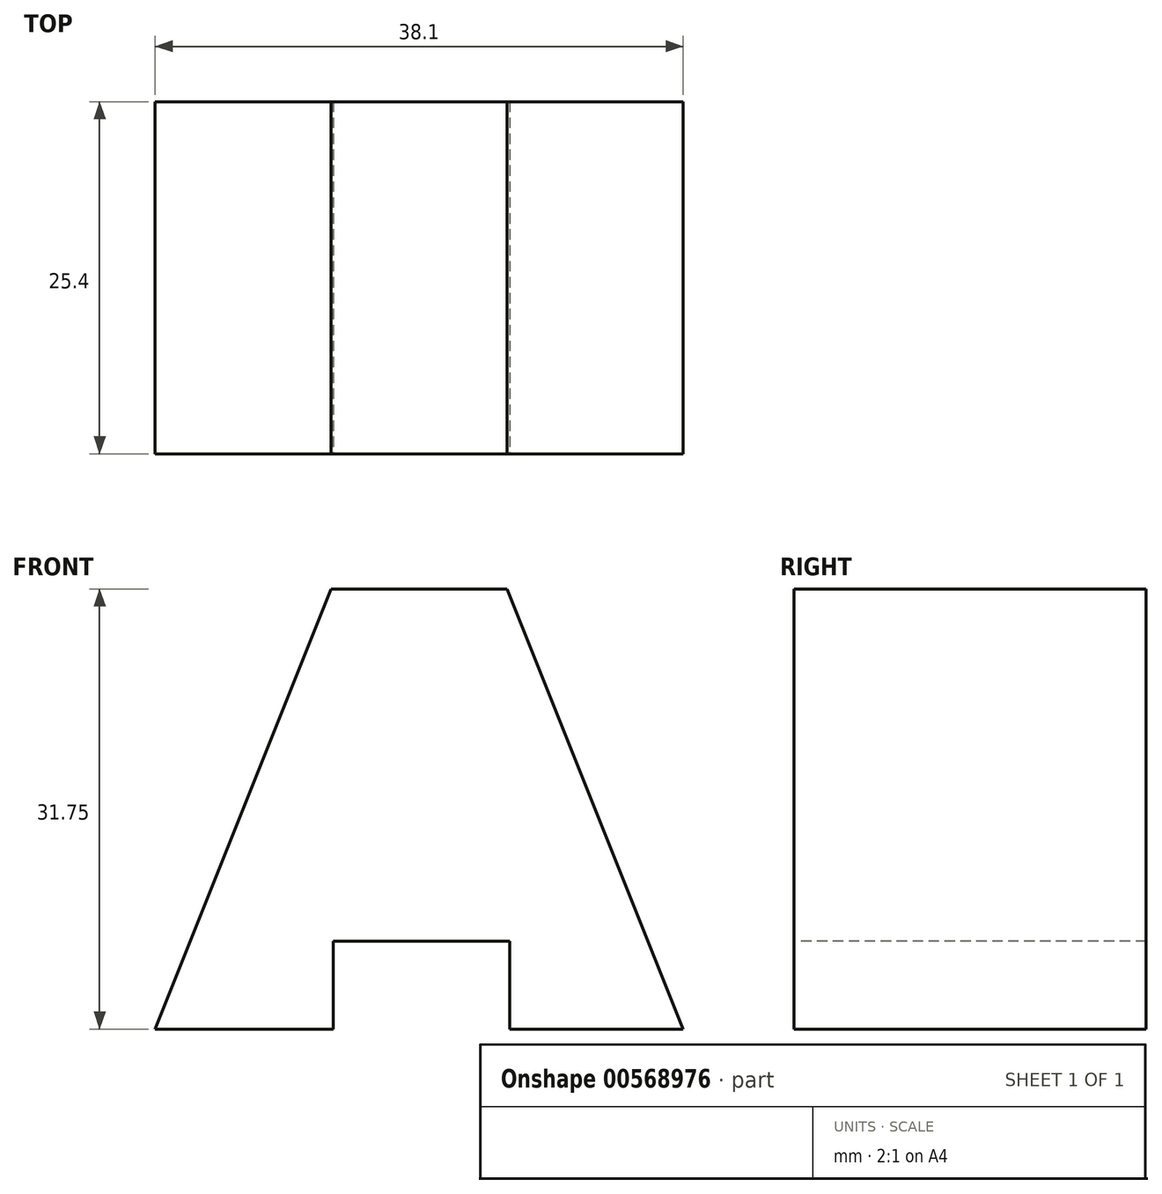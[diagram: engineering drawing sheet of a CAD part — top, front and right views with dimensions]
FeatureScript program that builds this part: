
annotation { "Feature Type Name" : "Feature", "Feature Type Description" : "" }
export const myFeature = defineFeature(function(context is Context, id is Id, definition is map)
    precondition{}
    {
        {
            var Q0;
            Q0=qCreatedBy(makeId("Front.planeOp"),FACE);
            var sketch = newSketch(context, id + "F0", { "sketchPlane" : qUnion([Q0])});
            skLineSegment(sketch, "E0.bottom", {"start": v(-30.4, 31.75) * mm, "end": v(7.7, 31.75) * mm});
            skLineSegment(sketch, "E0.top", {"start": v(-30.4, 0) * mm, "end": v(7.7, 0) * mm});
            skLineSegment(sketch, "E0.left", {"start": v(-30.4, 31.75) * mm, "end": v(-30.4, 0) * mm});
            skLineSegment(sketch, "E0.right", {"start": v(7.7, 31.75) * mm, "end": v(7.7, 0) * mm});
            skSolve(sketch);
        }
        {
            var Q0;
            Q0 = qSketchRegion(id + "F0", true);
            extrude(context, id + "F1", {"entities" : qUnion([Q0]), "depth" : 25.4 * mm, "offsetDistance" : 25.4 * mm});
        }
        {
            var Q0;
            Q0=makeQuery(id+"F1.opExtrude","CAP_FACE",FACE,{"disambiguationData":[OSD([sQuery(id+"F0.wireOp",EDGE,"E0.bottom"),sQuery(id+"F0.wireOp",EDGE,"E0.top"),sQuery(id+"F0.wireOp",EDGE,"E0.left"),sQuery(id+"F0.wireOp",EDGE,"E0.right")])],"isStart":false});
            var sketch = newSketch(context, id + "F2", { "sketchPlane" : qUnion([Q0])});
            skLineSegment(sketch, "E1", {"start": v(-5, 31.75) * mm, "end": v(7.7, 0) * mm});
            skLineSegment(sketch, "E2", {"start": v(7.7, 0) * mm, "end": v(7.7, 31.75) * mm});
            skLineSegment(sketch, "E3", {"start": v(7.7, 31.75) * mm, "end": v(-5, 31.75) * mm});
            skLineSegment(sketch, "E4", {"start": v(-17.7, 31.75) * mm, "end": v(-30.4, 0) * mm});
            skLineSegment(sketch, "E5", {"start": v(-30.4, 0) * mm, "end": v(-30.4, 31.75) * mm});
            skLineSegment(sketch, "E6", {"start": v(-30.4, 31.75) * mm, "end": v(-17.7, 31.75) * mm});
            skSolve(sketch);
        }
        {
            var Q0;
            Q0=makeQuery(id+"F2.imprint","IMPRINT",FACE,{"disambiguationData":[TD([[makeQuery(id+"F2.imprint","IMPRINT",EDGE,{"derivedFrom":sQuery(id+"F2.wireOp",EDGE,"E4")}),-1.0]])]});
            extrude(context, id + "F3", {"entities" : qUnion([Q0]), "operationType" : NewBodyOperationType.REMOVE, "oppositeDirection" : true, "depth" : 25.4 * mm, "offsetDistance" : 25.4 * mm});
        }
        {
            var Q0;
            Q0=makeQuery(id+"F1.opExtrude","CAP_FACE",FACE,{"disambiguationData":[OSD([sQuery(id+"F0.wireOp",EDGE,"E0.bottom"),sQuery(id+"F0.wireOp",EDGE,"E0.top"),sQuery(id+"F0.wireOp",EDGE,"E0.left"),sQuery(id+"F0.wireOp",EDGE,"E0.right")])],"isStart":false});
            var sketch = newSketch(context, id + "F4", { "sketchPlane" : qUnion([Q0])});
            skLineSegment(sketch, "E7", {"start": v(-5, 31.75) * mm, "end": v(7.7, 0) * mm});
            skLineSegment(sketch, "E8", {"start": v(7.7, 0) * mm, "end": v(7.7, 31.75) * mm});
            skLineSegment(sketch, "E9", {"start": v(7.7, 31.75) * mm, "end": v(-5, 31.75) * mm});
            skSolve(sketch);
        }
        {
            var Q0;
            Q0 = qSketchRegion(id + "F4", true);
            extrude(context, id + "F5", {"entities" : qUnion([Q0]), "operationType" : NewBodyOperationType.REMOVE, "oppositeDirection" : true, "depth" : 25.4 * mm, "offsetDistance" : 25.4 * mm});
        }
        {
            var Q0;
            Q0=makeQuery(id+"F1.opExtrude","CAP_FACE",FACE,{"disambiguationData":[OSD([sQuery(id+"F0.wireOp",EDGE,"E0.bottom"),sQuery(id+"F0.wireOp",EDGE,"E0.top"),sQuery(id+"F0.wireOp",EDGE,"E0.left"),sQuery(id+"F0.wireOp",EDGE,"E0.right")])],"isStart":false});
            var sketch = newSketch(context, id + "F6", { "sketchPlane" : qUnion([Q0])});
            skLineSegment(sketch, "E10", {"start": v(-17.53, 0) * mm, "end": v(-17.53, 6.35) * mm});
            skLineSegment(sketch, "E11", {"start": v(-17.53, 6.35) * mm, "end": v(-4.83, 6.35) * mm});
            skLineSegment(sketch, "E12", {"start": v(-4.83, 6.35) * mm, "end": v(-4.83, 0) * mm});
            skSolve(sketch);
        }
        {
            var Q0;
            {var subQ0=sQuery(id+"F6.wireOp",EDGE,"E10");Q0=makeQuery(id+"F6.imprint","IMPRINT",FACE,{"disambiguationData":[TD([[makeQuery(id+"F6.imprint","IMPRINT",EDGE,{"derivedFrom":subQ0}),-1.0]])]});}
            var sketch = newSketch(context, id + "F7", { "sketchPlane" : qUnion([Q0])});
            skSolve(sketch);
        }
        {
            var Q0;
            Q0 = qSketchRegion(id + "F7", true);
            var Q1;
            {var subQ0=sQuery(id+"F6.wireOp",EDGE,"E10");Q1=makeQuery(id+"F6.imprint","IMPRINT",FACE,{"disambiguationData":[TD([[makeQuery(id+"F6.imprint","IMPRINT",EDGE,{"derivedFrom":subQ0}),-1.0]])]});}
            extrude(context, id + "F8", {"entities" : qUnion([Q0, Q1]), "operationType" : NewBodyOperationType.REMOVE, "oppositeDirection" : true, "depth" : 25.4 * mm, "offsetDistance" : 25.4 * mm});
        }
    });
